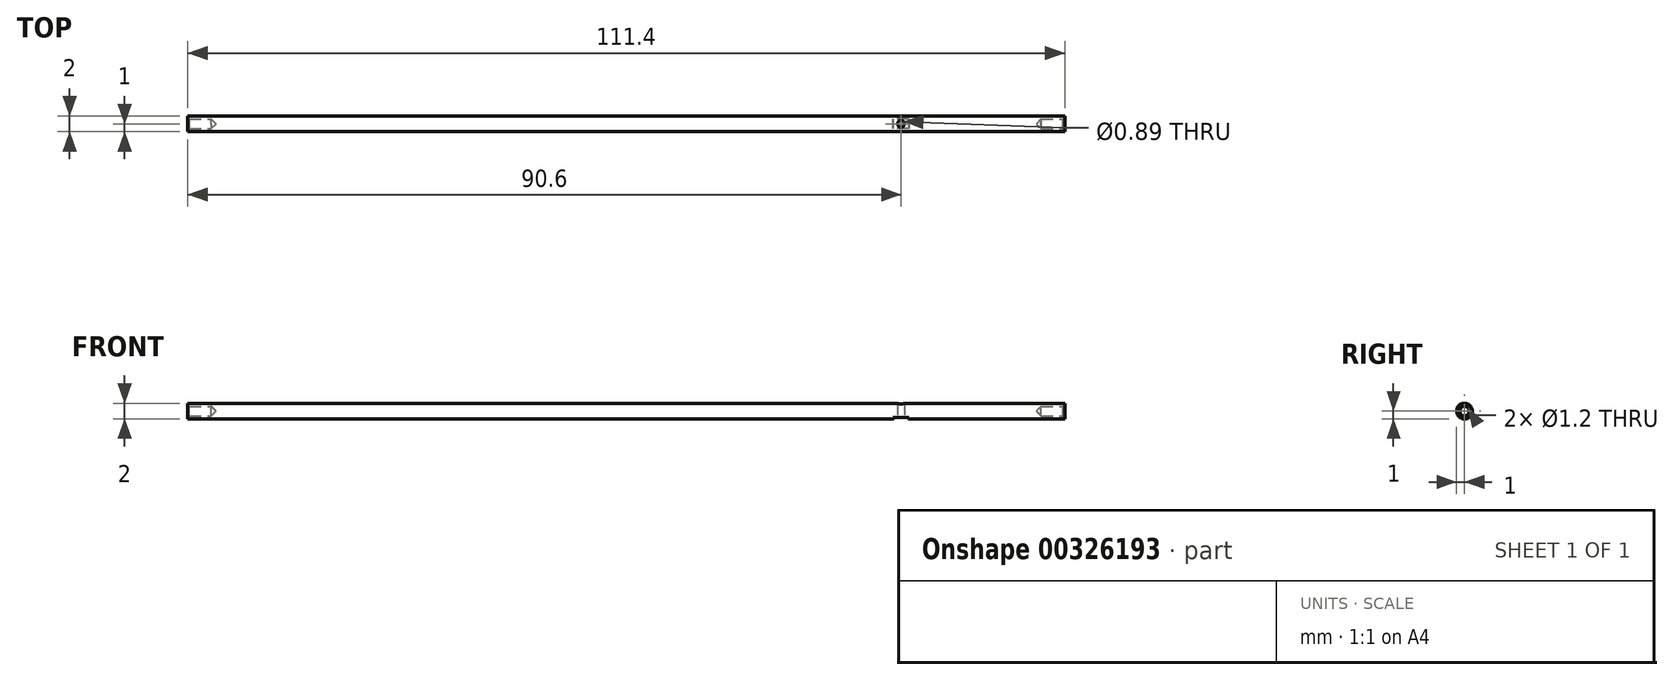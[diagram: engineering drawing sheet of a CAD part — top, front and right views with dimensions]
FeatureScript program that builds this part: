
annotation { "Feature Type Name" : "Feature", "Feature Type Description" : "" }
export const myFeature = defineFeature(function(context is Context, id is Id, definition is map)
    precondition{}
    {
        {
            var Q0;
            Q0=qCreatedBy(makeId("Right.planeOp"),FACE);
            var sketch = newSketch(context, id + "F0", { "sketchPlane" : qUnion([Q0])});
            skCircle(sketch, "E0", {"center": v(0, 0) * mm, "radius": 1 * mm});
            skSolve(sketch);
        }
        {
            var Q0;
            Q0=makeQuery(id+"F0.imprint","IMPRINT",FACE,{"disambiguationData":[TD([[makeQuery(id+"F0.imprint","IMPRINT",EDGE,{"derivedFrom":sQuery(id+"F0.wireOp",EDGE,"E0")}),1.0]])]});
            extrude(context, id + "F1", {"entities" : qUnion([Q0]), "depth" : 111.4 * mm});
        }
        {
            var Q0;
            Q0=qCreatedBy(makeId("Front.planeOp"),FACE);
            var sketch = newSketch(context, id + "F2", { "sketchPlane" : qUnion([Q0])});
            skLineSegment(sketch, "E1", {"start": v(0, 0) * mm, "end": v(111.4, 0) * mm, "construction": true});
            skLineSegment(sketch, "E2.bottom", {"start": v(91.6, -1.8) * mm, "end": v(89.6, -1.8) * mm});
            skLineSegment(sketch, "E2.top", {"start": v(91.6, -0.8) * mm, "end": v(89.6, -0.8) * mm});
            skLineSegment(sketch, "E2.left", {"start": v(91.6, -1.8) * mm, "end": v(91.6, -0.8) * mm});
            skLineSegment(sketch, "E2.right", {"start": v(89.6, -1.8) * mm, "end": v(89.6, -0.8) * mm});
            skSolve(sketch);
        }
        {
            var Q0;
            Q0=makeQuery(id+"F2.imprint","IMPRINT",FACE,{"disambiguationData":[TD([[makeQuery(id+"F2.imprint","IMPRINT",EDGE,{"derivedFrom":sQuery(id+"F2.wireOp",EDGE,"ZLbWFfED-z3We-k75V-j2rq-Yilhq1ERSvfZ.bottom")}),1.0]])]});
            var Q1;
            Q1=makeQuery(id+"F2.imprint","IMPRINT",FACE,{"disambiguationData":[TD([[makeQuery(id+"F2.imprint","IMPRINT",EDGE,{"derivedFrom":sQuery(id+"F2.wireOp",EDGE,"s18fpwNs-CyeE-Vpu6-Iavl-Q88z7r2e1Sys.bottom")}),-1.0]])]});
            var Q2;
            Q2=makeQuery(id+"F2.imprint","IMPRINT",FACE,{"disambiguationData":[TD([[makeQuery(id+"F2.imprint","IMPRINT",EDGE,{"derivedFrom":sQuery(id+"F2.wireOp",EDGE,"E2.bottom")}),-1.0]])]});
            extrude(context, id + "F3", {"entities" : qUnion([Q0, Q1, Q2]), "operationType" : NewBodyOperationType.REMOVE, "oppositeDirection" : true, "depth" : 5 * mm, "hasSecondDirection" : true, "secondDirectionOppositeDirection" : false, "secondDirectionDepth" : 25 * mm, "symmetric" : true});
        }
        {
            var Q0;
            Q0=qCreatedBy(makeId("Front.planeOp"),FACE);
            var sketch = newSketch(context, id + "F4", { "sketchPlane" : qUnion([Q0])});
            skLineSegment(sketch, "E3", {"start": v(0, 0) * mm, "end": v(111.4, 0) * mm, "construction": true});
            skLineSegment(sketch, "E4", {"start": v(111.4, 0) * mm, "end": v(111.4, -0.8) * mm});
            skLineSegment(sketch, "E5", {"start": v(111.2, -0.6) * mm, "end": v(108.4, -0.6) * mm});
            skLineSegment(sketch, "E6", {"start": v(108.4, -0.6) * mm, "end": v(107.8, 0) * mm});
            skLineSegment(sketch, "E7", {"start": v(107.8, 0) * mm, "end": v(111.4, 0) * mm});
            skLineSegment(sketch, "E8", {"start": v(111.2, -0.6) * mm, "end": v(111.4, -0.8) * mm});
            skLineSegment(sketch, "E9", {"start": v(55.7, 0) * mm, "end": v(55.7, -7.36) * mm, "construction": true});
            skLineSegment(sketch, "E10.MirrorCS", {"start": v(3, -0.6) * mm, "end": v(3.6, 0) * mm});
            skLineSegment(sketch, "E11.MirrorCS", {"start": v(0.2, -0.6) * mm, "end": v(3, -0.6) * mm});
            skLineSegment(sketch, "E12.MirrorCS", {"start": v(0.2, -0.6) * mm, "end": v(0, -0.8) * mm});
            skLineSegment(sketch, "E13.MirrorCS", {"start": v(0, 0) * mm, "end": v(0, -0.8) * mm});
            skLineSegment(sketch, "E14", {"start": v(3.6, 0) * mm, "end": v(0, 0) * mm});
            skSolve(sketch);
        }
        {
            var Q0;
            Q0 = qSketchRegion(id + "F4", true);
            var Q1;
            Q1=sQuery(id+"F4.wireOp",EDGE,"E3");
            revolve(context, id + "F5", {"operationType" : NewBodyOperationType.REMOVE, "entities" : qUnion([Q0]), "axis" : qUnion([Q1]), "revolveType" : RevolveType.FULL, "oppositeDirection" : true});
        }
        {
            var Q0;
            Q0=makeQuery(id+"F3.boolean.opBoolean","COPY",FACE,{"derivedFrom":makeQuery(id+"F3.opExtrude","SWEPT_FACE",FACE,{"disambiguationData":[OSD([sQuery(id+"F2.wireOp",EDGE,"E2.top")])]})});
            var sketch = newSketch(context, id + "F6", { "sketchPlane" : qUnion([Q0])});
            skCircle(sketch, "E15", {"center": v(90.6, 0) * mm, "radius": 0.44 * mm});
            skLineSegment(sketch, "E16", {"start": v(90.6, 0.6) * mm, "end": v(90.6, -0.6) * mm, "construction": true});
            skSolve(sketch);
        }
        {
            var Q0;
            Q0=makeQuery(id+"F6.imprint","IMPRINT",FACE,{"disambiguationData":[TD([[makeQuery(id+"F6.imprint","IMPRINT",EDGE,{"derivedFrom":sQuery(id+"F6.wireOp",EDGE,"E15")}),1.0]])]});
            extrude(context, id + "F7", {"entities" : qUnion([Q0]), "operationType" : NewBodyOperationType.REMOVE, "oppositeDirection" : true, "depth" : 25 * mm});
        }
    });
